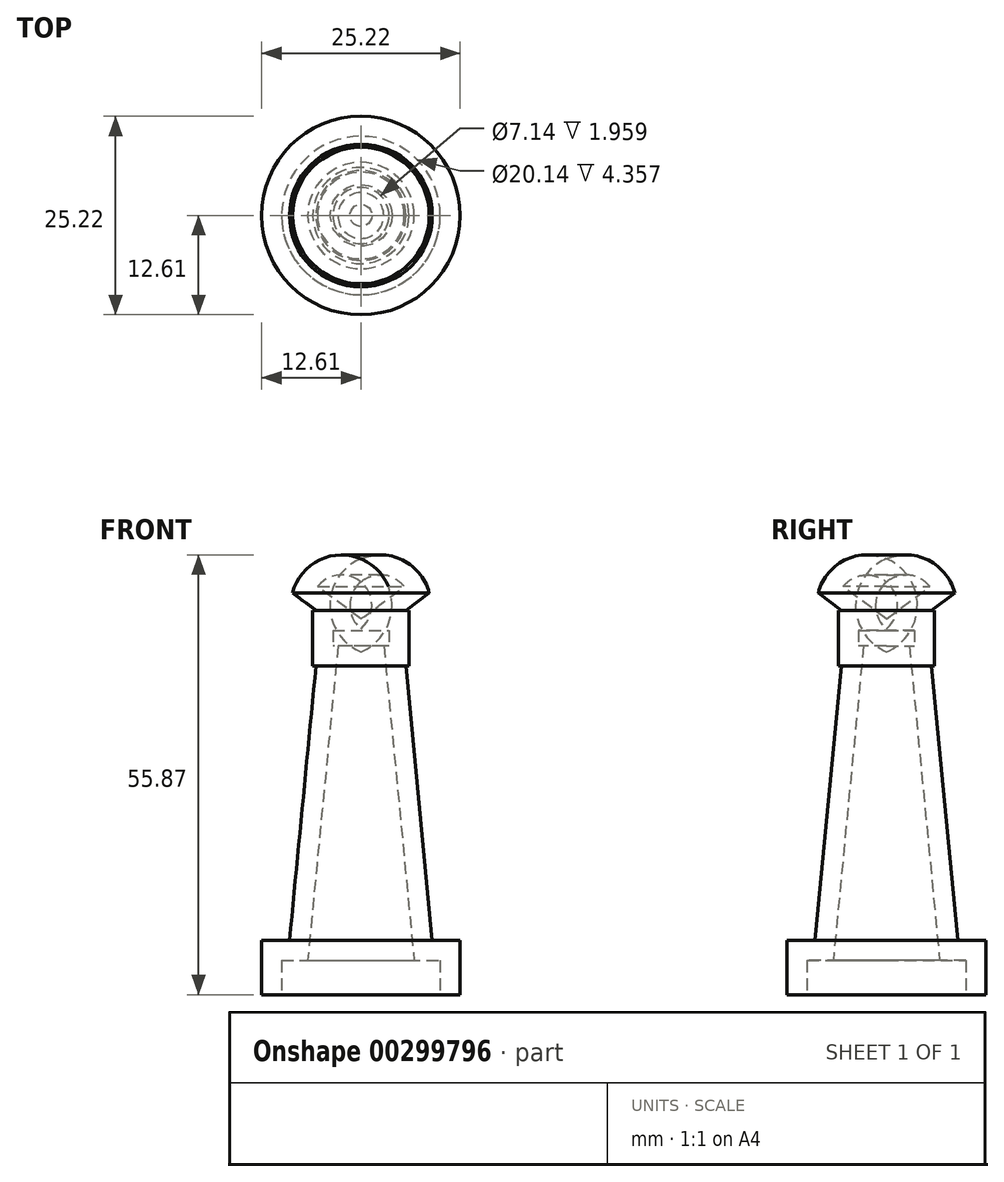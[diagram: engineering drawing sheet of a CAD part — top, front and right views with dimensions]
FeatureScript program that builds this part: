
annotation { "Feature Type Name" : "Feature", "Feature Type Description" : "" }
export const myFeature = defineFeature(function(context is Context, id is Id, definition is map)
    precondition{}
    {
        {
            var Q0;
            Q0=qCreatedBy(makeId("Front.planeOp"),FACE);
            var sketch = newSketch(context, id + "F0", { "sketchPlane" : qUnion([Q0])});
            skLineSegment(sketch, "E0", {"start": v(0, 0) * mm, "end": v(0, 55.38) * mm});
            skLineSegment(sketch, "E1", {"start": v(-8.67, 51.04) * mm, "end": v(-5.7, 48.82) * mm});
            skLineSegment(sketch, "E2", {"start": v(-5.7, 48.82) * mm, "end": v(-6.1, 48.82) * mm});
            skLineSegment(sketch, "E3", {"start": v(-6.1, 48.82) * mm, "end": v(-6.1, 41.78) * mm});
            skLineSegment(sketch, "E4", {"start": v(-6.1, 41.78) * mm, "end": v(-5.7, 41.78) * mm});
            skLineSegment(sketch, "E5", {"start": v(-5.7, 41.78) * mm, "end": v(-9.07, 6.9) * mm});
            skLineSegment(sketch, "E6", {"start": v(-9.07, 6.9) * mm, "end": v(-12.61, 6.9) * mm});
            skLineSegment(sketch, "E7", {"start": v(-12.61, 6.9) * mm, "end": v(-12.61, 0) * mm});
            skLineSegment(sketch, "E8", {"start": v(-12.61, 0) * mm, "end": v(0, 0) * mm});
            skArc(sketch, "E9", {"start": v(0, 55.38) * mm, "mid": v(-5.33, 55.2) * mm, "end": v(-8.67, 51.04) * mm});
            skSolve(sketch);
        }
        {
            var Q0;
            Q0=makeQuery(id+"F0.imprint","IMPRINT",FACE,{"disambiguationData":[TD([[makeQuery(id+"F0.imprint","IMPRINT",EDGE,{"derivedFrom":sQuery(id+"F0.wireOp",EDGE,"E0")}),1.0]])]});
            var Q1;
            Q1=sQuery(id+"F0.wireOp",EDGE,"E0");
            revolve(context, id + "F1", {"entities" : qUnion([Q0]), "axis" : qUnion([Q1]), "revolveType" : RevolveType.FULL});
        }
        {
            var Q0;
            Q0=makeQuery(id+"F1.opRevolve","SWEPT_FACE",FACE,{"disambiguationData":[OSD([sQuery(id+"F0.wireOp",EDGE,"E8")])]});
            shell(context, id + "F2", {"entities" : qUnion([Q0]), "thickness" : 2.54 * mm});
        }
    });
